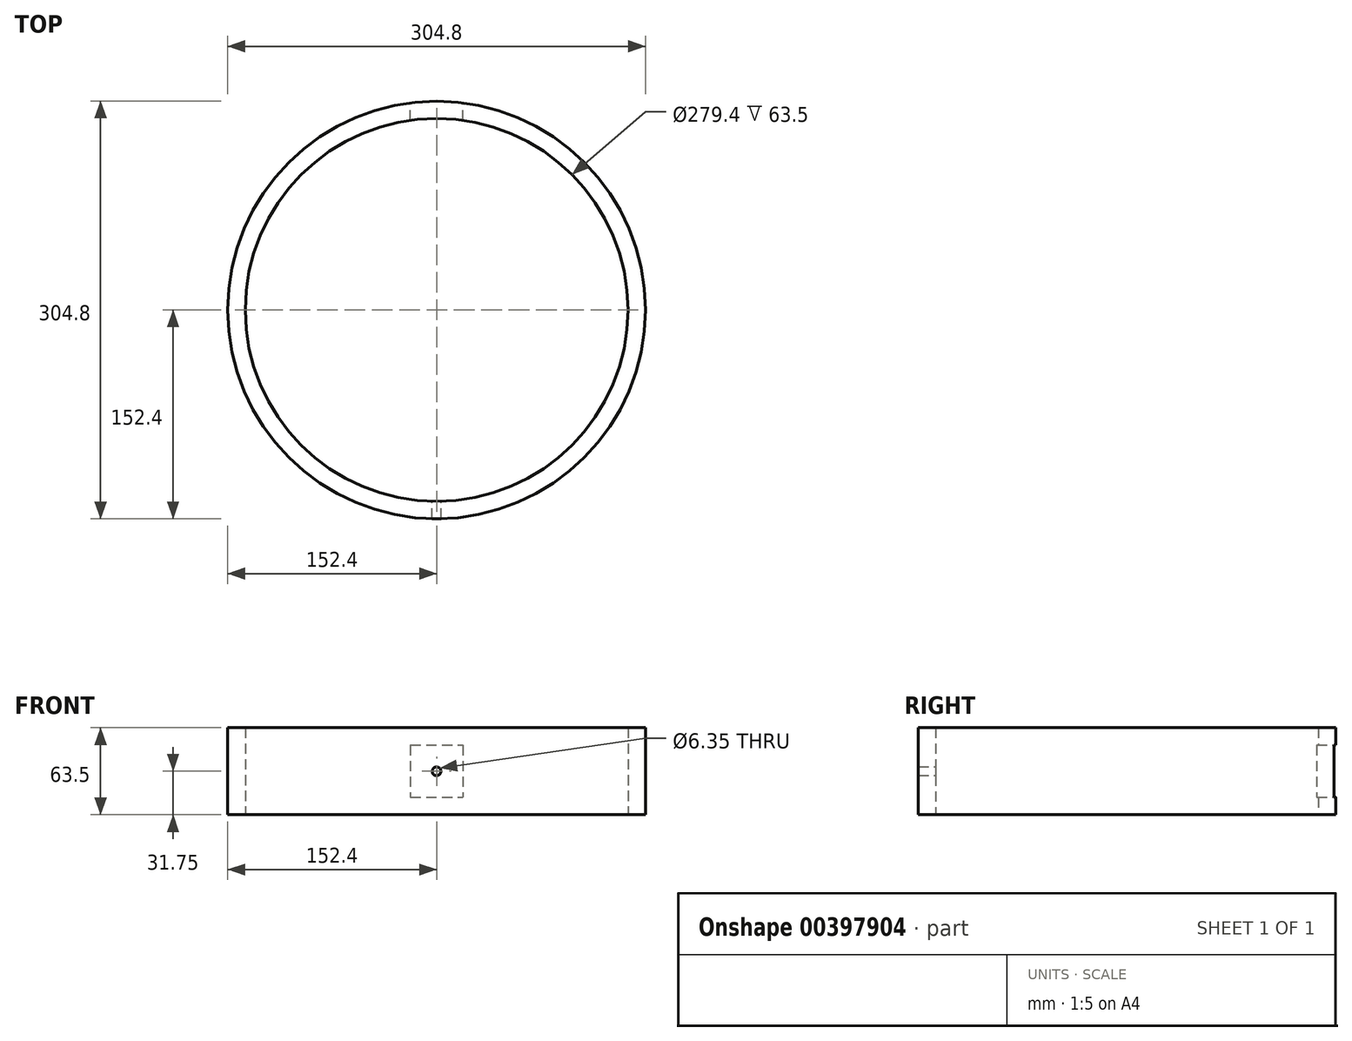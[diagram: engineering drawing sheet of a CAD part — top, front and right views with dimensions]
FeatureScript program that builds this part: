
annotation { "Feature Type Name" : "Feature", "Feature Type Description" : "" }
export const myFeature = defineFeature(function(context is Context, id is Id, definition is map)
    precondition{}
    {
        {
            var Q0;
            Q0=qCreatedBy(makeId("Top.planeOp"),FACE);
            var sketch = newSketch(context, id + "F0", { "sketchPlane" : qUnion([Q0])});
            skLineSegment(sketch, "E0.bottom", {"start": v(152.4, 152.4) * mm, "end": v(-152.4, 152.4) * mm});
            skLineSegment(sketch, "E0.top", {"start": v(152.4, -152.4) * mm, "end": v(-152.4, -152.4) * mm});
            skLineSegment(sketch, "E0.left", {"start": v(152.4, 152.4) * mm, "end": v(152.4, -152.4) * mm});
            skLineSegment(sketch, "E0.right", {"start": v(-152.4, 152.4) * mm, "end": v(-152.4, -152.4) * mm});
            skPoint(sketch, "E0.middle", {"position": v(0, 0) * mm});
            skCircle(sketch, "E1", {"center": v(0, 0) * mm, "radius": 139.7 * mm});
            skSolve(sketch);
        }
        {
            var Q0;
            Q0=makeQuery(id+"F0.imprint","IMPRINT",FACE,{"disambiguationData":[TD([[makeQuery(id+"F0.imprint","IMPRINT",EDGE,{"derivedFrom":sQuery(id+"F0.wireOp",EDGE,"E0.bottom")}),1.0]])]});
            extrude(context, id + "F1", {"entities" : qUnion([Q0]), "depth" : 63.5 * mm});
        }
        {
            var Q0;
            Q0=makeQuery(id+"F1.opExtrude","SWEPT_FACE",FACE,{"disambiguationData":[OSD([sQuery(id+"F0.wireOp",EDGE,"E0.bottom")])]});
            var sketch = newSketch(context, id + "F2", { "sketchPlane" : qUnion([Q0])});
            skLineSegment(sketch, "E2", {"start": v(152.4, 63.5) * mm, "end": v(0, 63.5) * mm, "construction": true});
            skLineSegment(sketch, "E3", {"start": v(0, 63.5) * mm, "end": v(0, 0) * mm, "construction": true});
            skLineSegment(sketch, "E4", {"start": v(0, 0) * mm, "end": v(0, 31.75) * mm, "construction": true});
            skLineSegment(sketch, "E5.bottom", {"start": v(-19.05, 12.7) * mm, "end": v(19.05, 12.7) * mm});
            skLineSegment(sketch, "E5.top", {"start": v(-19.05, 50.8) * mm, "end": v(19.05, 50.8) * mm});
            skLineSegment(sketch, "E5.left", {"start": v(-19.05, 12.7) * mm, "end": v(-19.05, 50.8) * mm});
            skLineSegment(sketch, "E5.right", {"start": v(19.05, 12.7) * mm, "end": v(19.05, 50.8) * mm});
            skPoint(sketch, "E5.middle", {"position": v(0, 31.75) * mm});
            skCircle(sketch, "E6", {"center": v(0, 31.75) * mm, "radius": 1.59 * mm});
            skSolve(sketch);
        }
        {
            var Q0;
            Q0=sQuery(id+"F2.wireOp",VERTEX,"E5.middle");
            var Q1;
            Q1=makeQuery(id+"F4.boolean.opBoolean","SPLIT",BODY,{"disambiguationData":[OD(0.0)],"derivedFrom":makeQuery(id+"F1.opExtrude","SWEPT_BODY",BODY,{"disambiguationData":[OSD([sQuery(id+"F0.wireOp",EDGE,"E0.bottom"),sQuery(id+"F0.wireOp",EDGE,"E0.top"),sQuery(id+"F0.wireOp",EDGE,"E0.left"),sQuery(id+"F0.wireOp",EDGE,"E0.right"),sQuery(id+"F0.wireOp",EDGE,"E1")])]})});
            var Q2;
            Q2=makeQuery(id+"F4.boolean.opBoolean","SPLIT",BODY,{"disambiguationData":[OD(1.0)],"derivedFrom":makeQuery(id+"F1.opExtrude","SWEPT_BODY",BODY,{"disambiguationData":[OSD([sQuery(id+"F0.wireOp",EDGE,"E0.bottom"),sQuery(id+"F0.wireOp",EDGE,"E0.top"),sQuery(id+"F0.wireOp",EDGE,"E0.left"),sQuery(id+"F0.wireOp",EDGE,"E0.right"),sQuery(id+"F0.wireOp",EDGE,"E1")])]})});
            hole(context, id + "F3", {"style" : HoleStyle.SIMPLE, "endStyle" : HoleEndStyle.THROUGH, "holeDiameter" : 6.35 * mm, "isTappedThrough" : true, "tappedDepth" : 12.7 * mm, "tapClearance" : 3, "locations" : qUnion([Q0]), "scope" : qUnion([Q1, Q2])});
        }
        {
            var Q0;
            Q0=makeQuery(id+"F2.imprint","IMPRINT",FACE,{"disambiguationData":[TD([[makeQuery(id+"F2.imprint","IMPRINT",EDGE,{"derivedFrom":sQuery(id+"F2.wireOp",EDGE,"E5.bottom")}),1.0]])]});
            extrude(context, id + "F4", {"entities" : qUnion([Q0]), "operationType" : NewBodyOperationType.REMOVE, "oppositeDirection" : true, "depth" : 25.4 * mm});
        }
        {
            var Q0;
            Q0=makeQuery(id+"F1.opExtrude","SWEPT_EDGE",EDGE,{"disambiguationData":[OSD([sQuery(id+"F0.wireOp",EDGE,"E0.bottom"),sQuery(id+"F0.wireOp",EDGE,"E0.right")])]});
            var Q1;
            Q1=makeQuery(id+"F1.opExtrude","SWEPT_EDGE",EDGE,{"disambiguationData":[OSD([sQuery(id+"F0.wireOp",EDGE,"E0.bottom"),sQuery(id+"F0.wireOp",EDGE,"E0.left")])]});
            var Q2;
            Q2=makeQuery(id+"F1.opExtrude","SWEPT_EDGE",EDGE,{"disambiguationData":[OSD([sQuery(id+"F0.wireOp",EDGE,"E0.top"),sQuery(id+"F0.wireOp",EDGE,"E0.left")])]});
            var Q3;
            Q3=makeQuery(id+"F1.opExtrude","SWEPT_EDGE",EDGE,{"disambiguationData":[OSD([sQuery(id+"F0.wireOp",EDGE,"E0.top"),sQuery(id+"F0.wireOp",EDGE,"E0.right")])]});
            fillet(context, id + "F5", {"entities" : qUnion([Q0, Q1, Q2, Q3]), "radius" : 152.4 * mm, "tangentPropagation" : true, "allowEdgeOverflow" : false});
        }
    });
